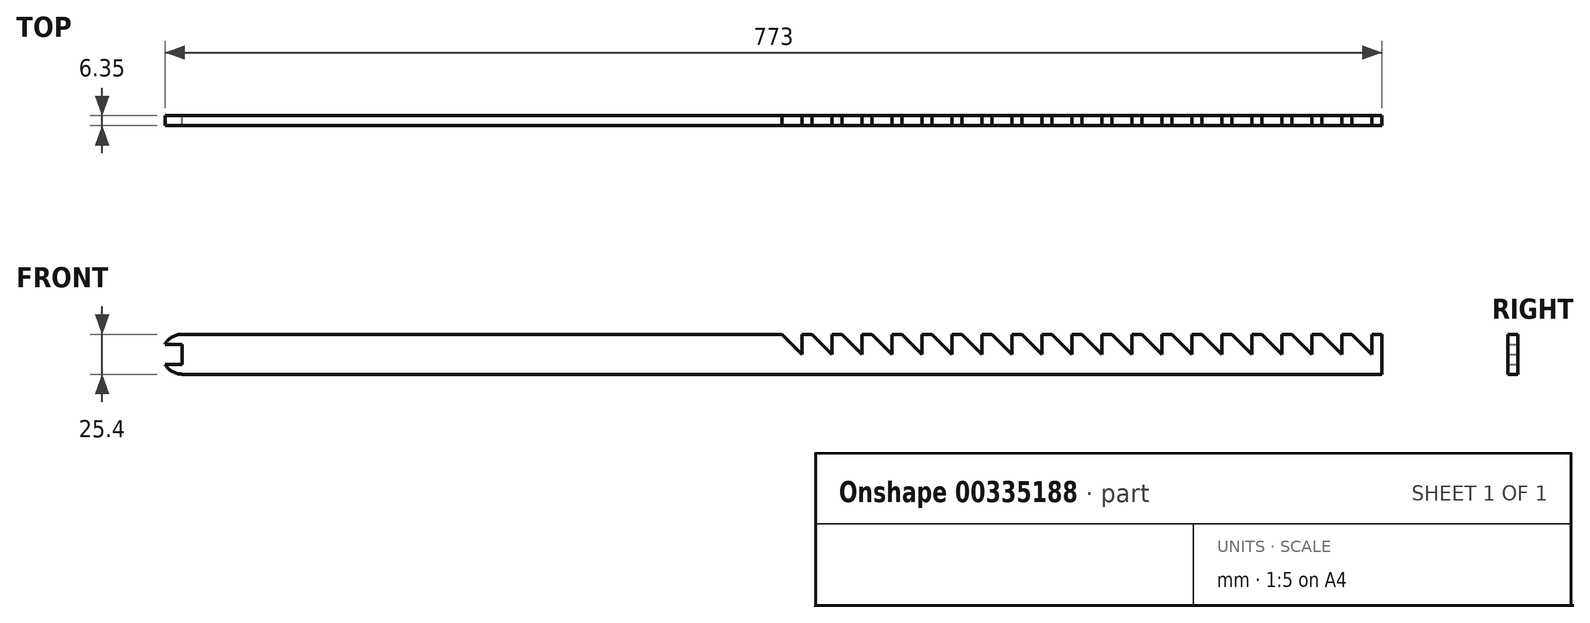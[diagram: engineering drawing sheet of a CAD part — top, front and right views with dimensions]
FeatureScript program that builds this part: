
annotation { "Feature Type Name" : "Feature", "Feature Type Description" : "" }
export const myFeature = defineFeature(function(context is Context, id is Id, definition is map)
    precondition{}
    {
        {
            var Q0;
            Q0=qCreatedBy(makeId("Front.planeOp"),FACE);
            var sketch = newSketch(context, id + "F0", { "sketchPlane" : qUnion([Q0])});
            skLineSegment(sketch, "E0.bottom", {"start": v(-381, 12.7) * mm, "end": v(381, 12.7) * mm});
            skLineSegment(sketch, "E0.top", {"start": v(-381, -12.7) * mm, "end": v(381, -12.7) * mm});
            skLineSegment(sketch, "E0.left", {"start": v(-381, 12.7) * mm, "end": v(-381, -12.7) * mm});
            skLineSegment(sketch, "E0.right", {"start": v(381, 12.7) * mm, "end": v(381, -12.7) * mm});
            skPoint(sketch, "E0.middle", {"position": v(0, 0) * mm});
            skArc(sketch, "E1", {"start": v(-381, 12.7) * mm, "mid": v(-393.7, 0) * mm, "end": v(-381, -12.7) * mm});
            skLineSegment(sketch, "E2", {"start": v(-386.23, 11.58) * mm, "end": v(-381, 6.35) * mm});
            skLineSegment(sketch, "E3", {"start": v(-381, -6.35) * mm, "end": v(-386.23, -11.58) * mm});
            skLineSegment(sketch, "E4", {"start": v(-381, -6.35) * mm, "end": v(-392, -6.35) * mm});
            skLineSegment(sketch, "E5", {"start": v(-381, 6.35) * mm, "end": v(-392, 6.35) * mm});
            skLineSegment(sketch, "E6", {"start": v(381, 0) * mm, "end": v(-393.7, 0) * mm, "construction": true});
            skPoint(sketch, "E7.orphan", {"position": v(-133.27, 6.35) * mm});
            skPoint(sketch, "E8.orphan", {"position": v(-133.27, 0) * mm});
            skLineSegment(sketch, "E9", {"start": v(-381, 12.7) * mm, "end": v(0, 12.7) * mm});
            skLineSegment(sketch, "E10", {"start": v(0, 12.7) * mm, "end": v(12.7, 0) * mm});
            skLineSegment(sketch, "E11", {"start": v(12.7, 0) * mm, "end": v(12.7, 12.7) * mm});
            skLineSegment(sketch, "E12", {"start": v(12.7, 12.7) * mm, "end": v(19.05, 12.7) * mm});
            skLineSegment(sketch, "E13", {"start": v(19.05, 12.7) * mm, "end": v(31.75, 0) * mm});
            skLineSegment(sketch, "E14", {"start": v(31.75, 0) * mm, "end": v(31.75, 12.7) * mm});
            skLineSegment(sketch, "E15", {"start": v(31.75, 12.7) * mm, "end": v(38.1, 12.7) * mm});
            skLineSegment(sketch, "E16", {"start": v(38.1, 12.7) * mm, "end": v(50.8, 0) * mm});
            skLineSegment(sketch, "E17", {"start": v(50.8, 0) * mm, "end": v(50.8, 12.7) * mm});
            skLineSegment(sketch, "E18", {"start": v(50.8, 12.7) * mm, "end": v(57.15, 12.7) * mm});
            skLineSegment(sketch, "E19", {"start": v(57.15, 12.7) * mm, "end": v(69.85, 0) * mm});
            skLineSegment(sketch, "E20", {"start": v(69.85, 0) * mm, "end": v(69.85, 12.7) * mm});
            skLineSegment(sketch, "E21", {"start": v(69.85, 12.7) * mm, "end": v(76.2, 12.7) * mm});
            skLineSegment(sketch, "E22", {"start": v(76.2, 12.7) * mm, "end": v(88.9, 0) * mm});
            skLineSegment(sketch, "E23", {"start": v(88.9, 0) * mm, "end": v(88.9, 12.7) * mm});
            skLineSegment(sketch, "E24", {"start": v(88.9, 12.7) * mm, "end": v(95.25, 12.7) * mm});
            skLineSegment(sketch, "E25", {"start": v(95.25, 12.7) * mm, "end": v(107.95, 0) * mm});
            skLineSegment(sketch, "E26", {"start": v(107.95, 0) * mm, "end": v(107.95, 12.7) * mm});
            skLineSegment(sketch, "E27", {"start": v(107.95, 12.7) * mm, "end": v(114.3, 12.7) * mm});
            skLineSegment(sketch, "E28", {"start": v(114.3, 12.7) * mm, "end": v(127, 0) * mm});
            skLineSegment(sketch, "E29", {"start": v(127, 0) * mm, "end": v(127, 12.7) * mm});
            skLineSegment(sketch, "E30", {"start": v(127, 12.7) * mm, "end": v(133.35, 12.7) * mm});
            skLineSegment(sketch, "E31", {"start": v(133.35, 12.7) * mm, "end": v(146.05, 0) * mm});
            skLineSegment(sketch, "E32", {"start": v(146.05, 0) * mm, "end": v(146.05, 12.7) * mm});
            skLineSegment(sketch, "E33", {"start": v(146.05, 12.7) * mm, "end": v(152.4, 12.7) * mm});
            skLineSegment(sketch, "E34", {"start": v(152.4, 12.7) * mm, "end": v(165.1, 0) * mm});
            skLineSegment(sketch, "E35", {"start": v(165.1, 0) * mm, "end": v(165.1, 12.7) * mm});
            skLineSegment(sketch, "E36", {"start": v(165.1, 12.7) * mm, "end": v(171.45, 12.7) * mm});
            skLineSegment(sketch, "E37", {"start": v(171.45, 12.7) * mm, "end": v(184.15, 0) * mm});
            skLineSegment(sketch, "E38", {"start": v(184.15, 0) * mm, "end": v(184.15, 12.7) * mm});
            skLineSegment(sketch, "E39", {"start": v(184.15, 12.7) * mm, "end": v(190.5, 12.7) * mm});
            skLineSegment(sketch, "E40", {"start": v(190.5, 12.7) * mm, "end": v(203.2, 0) * mm});
            skLineSegment(sketch, "E41", {"start": v(203.2, 0) * mm, "end": v(203.2, 12.7) * mm});
            skLineSegment(sketch, "E42", {"start": v(203.2, 12.7) * mm, "end": v(209.55, 12.7) * mm});
            skLineSegment(sketch, "E43", {"start": v(209.55, 12.7) * mm, "end": v(222.25, 0) * mm});
            skLineSegment(sketch, "E44", {"start": v(222.25, 0) * mm, "end": v(222.25, 12.7) * mm});
            skLineSegment(sketch, "E45", {"start": v(222.25, 12.7) * mm, "end": v(228.6, 12.7) * mm});
            skLineSegment(sketch, "E46", {"start": v(228.6, 12.7) * mm, "end": v(241.3, 0) * mm});
            skLineSegment(sketch, "E47", {"start": v(241.3, 0) * mm, "end": v(241.3, 12.7) * mm});
            skLineSegment(sketch, "E48", {"start": v(241.3, 12.7) * mm, "end": v(247.65, 12.7) * mm});
            skLineSegment(sketch, "E49", {"start": v(247.65, 12.7) * mm, "end": v(260.35, 0) * mm});
            skLineSegment(sketch, "E50", {"start": v(260.35, 0) * mm, "end": v(260.35, 12.7) * mm});
            skLineSegment(sketch, "E51", {"start": v(260.35, 12.7) * mm, "end": v(266.7, 12.7) * mm});
            skLineSegment(sketch, "E52", {"start": v(266.7, 12.7) * mm, "end": v(279.4, 0) * mm});
            skLineSegment(sketch, "E53", {"start": v(279.4, 0) * mm, "end": v(279.4, 12.7) * mm});
            skLineSegment(sketch, "E54", {"start": v(279.4, 12.7) * mm, "end": v(285.75, 12.7) * mm});
            skLineSegment(sketch, "E55", {"start": v(285.75, 12.7) * mm, "end": v(298.45, 0) * mm});
            skLineSegment(sketch, "E56", {"start": v(298.45, 0) * mm, "end": v(298.45, 12.7) * mm});
            skLineSegment(sketch, "E57", {"start": v(298.45, 12.7) * mm, "end": v(304.8, 12.7) * mm});
            skLineSegment(sketch, "E58", {"start": v(304.8, 12.7) * mm, "end": v(317.5, 0) * mm});
            skLineSegment(sketch, "E59", {"start": v(317.5, 0) * mm, "end": v(317.5, 12.7) * mm});
            skLineSegment(sketch, "E60", {"start": v(317.5, 12.7) * mm, "end": v(323.85, 12.7) * mm});
            skLineSegment(sketch, "E61", {"start": v(323.85, 12.7) * mm, "end": v(336.55, 0) * mm});
            skLineSegment(sketch, "E62", {"start": v(336.55, 0) * mm, "end": v(336.55, 12.7) * mm});
            skLineSegment(sketch, "E63", {"start": v(336.55, 12.7) * mm, "end": v(342.9, 12.7) * mm});
            skLineSegment(sketch, "E64", {"start": v(342.9, 12.7) * mm, "end": v(355.6, 0) * mm});
            skLineSegment(sketch, "E65", {"start": v(355.6, 0) * mm, "end": v(355.6, 12.7) * mm});
            skLineSegment(sketch, "E66", {"start": v(355.6, 12.7) * mm, "end": v(361.95, 12.7) * mm});
            skLineSegment(sketch, "E67", {"start": v(361.95, 12.7) * mm, "end": v(374.65, 0) * mm});
            skLineSegment(sketch, "E68", {"start": v(374.65, 0) * mm, "end": v(374.65, 12.7) * mm});
            skLineSegment(sketch, "E69.bottom", {"start": v(-323.97, -12.7) * mm, "end": v(311.03, -12.7) * mm});
            skLineSegment(sketch, "E69.top", {"start": v(-323.97, -50.8) * mm, "end": v(311.03, -50.8) * mm});
            skLineSegment(sketch, "E69.left", {"start": v(-323.97, -12.7) * mm, "end": v(-323.97, -50.8) * mm});
            skLineSegment(sketch, "E69.right", {"start": v(311.03, -12.7) * mm, "end": v(311.03, -50.8) * mm});
            skLineSegment(sketch, "E70", {"start": v(-298.57, -50.8) * mm, "end": v(-298.57, -31.75) * mm});
            skPoint(sketch, "E70.endSnap0", {"position": v(-323.97, -31.75) * mm});
            skLineSegment(sketch, "E71", {"start": v(-298.57, -31.75) * mm, "end": v(-285.87, -31.75) * mm});
            skLineSegment(sketch, "E72", {"start": v(-285.87, -31.75) * mm, "end": v(-285.87, -50.8) * mm});
            skLineSegment(sketch, "E73", {"start": v(285.63, -50.8) * mm, "end": v(285.63, -31.75) * mm});
            skLineSegment(sketch, "E74", {"start": v(285.63, -31.75) * mm, "end": v(272.93, -31.75) * mm});
            skLineSegment(sketch, "E75", {"start": v(272.93, -31.75) * mm, "end": v(272.93, -50.8) * mm});
            skSolve(sketch);
        }
        {
            var Q0;
            {var subQ3=sQuery(id+"F0.wireOp",EDGE,"E2");Q0=makeQuery(id+"F0.imprint","IMPRINT",FACE,{"disambiguationData":[TD([[makeQuery(id+"F0.imprint","IMPRINT",EDGE,{"derivedFrom":subQ3}),1.0]])]});}
            var Q1;
            {var subQ3=sQuery(id+"F0.wireOp",EDGE,"E3");Q1=makeQuery(id+"F0.imprint","IMPRINT",FACE,{"disambiguationData":[TD([[makeQuery(id+"F0.imprint","IMPRINT",EDGE,{"derivedFrom":subQ3}),1.0]])]});}
            var Q2;
            {var subQ0=sQuery(id+"F0.wireOp",EDGE,"E2");Q2=makeQuery(id+"F0.imprint","IMPRINT",FACE,{"disambiguationData":[TD([[makeQuery(id+"F0.imprint","IMPRINT",EDGE,{"derivedFrom":subQ0}),-1.0]])]});}
            var Q3;
            {var subQ0=sQuery(id+"F0.wireOp",EDGE,"E3");Q3=makeQuery(id+"F0.imprint","IMPRINT",FACE,{"disambiguationData":[TD([[makeQuery(id+"F0.imprint","IMPRINT",EDGE,{"derivedFrom":subQ0}),-1.0]])]});}
            var Q4;
            Q4=makeQuery(id+"F0.imprint","IMPRINT",FACE,{"disambiguationData":[TD([[makeQuery(id+"F0.imprint","IMPRINT",EDGE,{"derivedFrom":sQuery(id+"F0.wireOp",EDGE,"E69.bottom")}),-1.0]])]});
            var Q5;
            {var subQ0=sQuery(id+"F0.wireOp",EDGE,"E0.right");Q5=makeQuery(id+"F0.imprint","IMPRINT",FACE,{"disambiguationData":[TD([[makeQuery(id+"F0.imprint","IMPRINT",EDGE,{"derivedFrom":subQ0}),-1.0]])]});}
            extrude(context, id + "F1", {"entities" : qUnion([Q0, Q1, Q2, Q3, Q4, Q5]), "depth" : 6.35 * mm});
        }
    });
